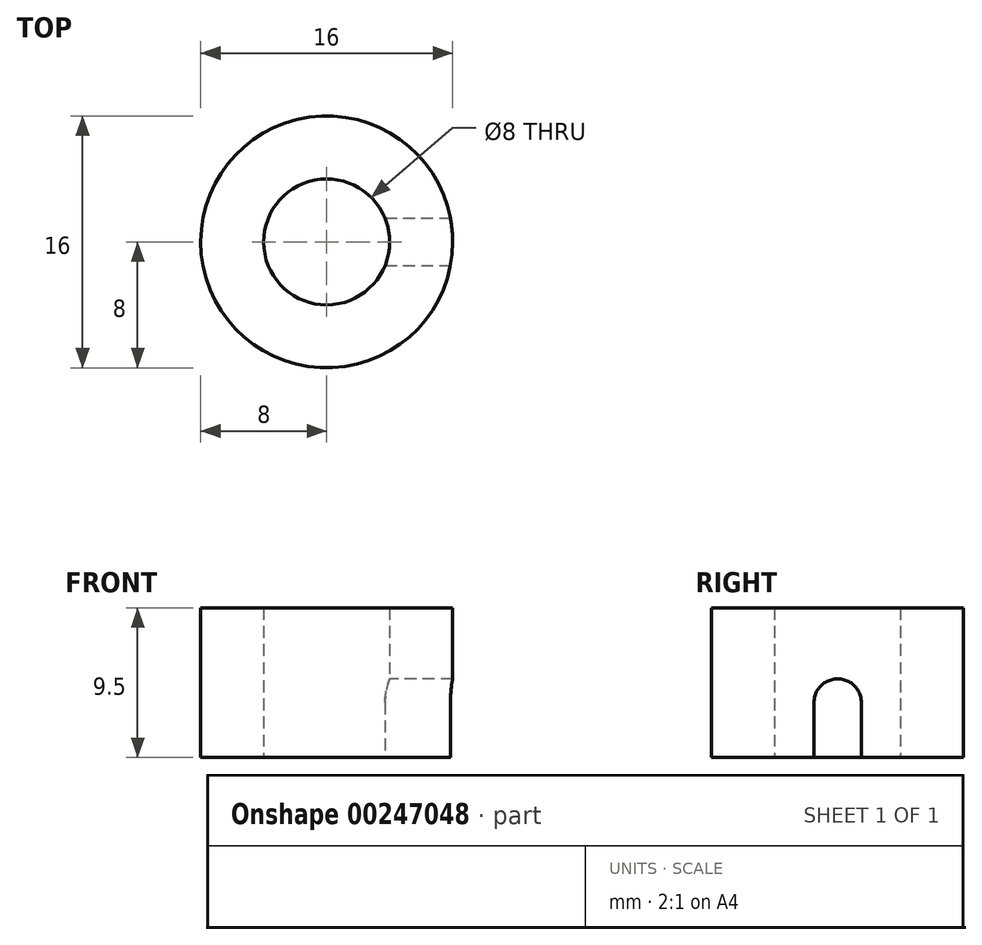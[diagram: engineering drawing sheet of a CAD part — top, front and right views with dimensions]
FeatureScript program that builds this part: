
annotation { "Feature Type Name" : "Feature", "Feature Type Description" : "" }
export const myFeature = defineFeature(function(context is Context, id is Id, definition is map)
    precondition{}
    {
        {
            var Q0;
            Q0=qCreatedBy(makeId("Top.planeOp"),FACE);
            var sketch = newSketch(context, id + "F0", { "sketchPlane" : qUnion([Q0])});
            skCircle(sketch, "E0", {"center": v(0, 0) * mm, "radius": 4 * mm});
            skCircle(sketch, "E1", {"center": v(0, 0) * mm, "radius": 8 * mm});
            skSolve(sketch);
        }
        {
            var Q0;
            Q0 = qSketchRegion(id + "F0", true);
            extrude(context, id + "F1", {"entities" : qUnion([Q0]), "depth" : 9.5 * mm});
        }
        {
            var Q0;
            Q0=makeQuery(id+"F1.opExtrude","CAP_FACE",FACE,{"disambiguationData":[OSD([sQuery(id+"F0.wireOp",EDGE,"E0"),sQuery(id+"F0.wireOp",EDGE,"E1")])],"isStart":true});
            var sketch = newSketch(context, id + "F2", { "sketchPlane" : qUnion([Q0])});
            skLineSegment(sketch, "E2.bottom", {"start": v(-0.98, 1.5) * mm, "end": v(13.18, 1.5) * mm});
            skLineSegment(sketch, "E2.top", {"start": v(-0.98, -1.5) * mm, "end": v(13.18, -1.5) * mm});
            skLineSegment(sketch, "E2.left", {"start": v(-0.98, 1.5) * mm, "end": v(-0.98, -1.5) * mm});
            skLineSegment(sketch, "E2.right", {"start": v(13.18, 1.5) * mm, "end": v(13.18, -1.5) * mm});
            skSolve(sketch);
        }
        {
            var Q0;
            Q0 = qSketchRegion(id + "F2", true);
            extrude(context, id + "F3", {"entities" : qUnion([Q0]), "operationType" : NewBodyOperationType.REMOVE, "oppositeDirection" : true, "depth" : 5 * mm});
        }
        {
            var Q0;
            Q0=makeQuery(id+"F3.boolean.opBoolean","COPY",EDGE,{"derivedFrom":makeQuery(id+"F3.opExtrude","CAP_EDGE",EDGE,{"disambiguationData":[OSD([sQuery(id+"F2.wireOp",EDGE,"E2.bottom")])],"isStart":false})});
            var Q1;
            Q1=makeQuery(id+"F3.boolean.opBoolean","COPY",EDGE,{"derivedFrom":makeQuery(id+"F3.opExtrude","CAP_EDGE",EDGE,{"disambiguationData":[OSD([sQuery(id+"F2.wireOp",EDGE,"E2.top")])],"isStart":false})});
            fillet(context, id + "F4", {"entities" : qUnion([Q0, Q1]), "radius" : 1.5 * mm, "tangentPropagation" : true, "allowEdgeOverflow" : false});
        }
    });
